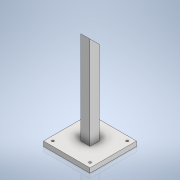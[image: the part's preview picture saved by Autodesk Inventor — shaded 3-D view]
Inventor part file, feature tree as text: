
AUTODESK INVENTOR PART (.ipt)
format: ipt  version: 2022 (Build 260153000, 153)  size: 131,584 bytes
history: native  units: mm
features: extrude x4, sketch x4
ambient origin geometry x8: Origin, YZ Plane, XZ Plane, XY Plane, X Axis, Y Axis, Z Axis, Center Point
bodies: Solid1 (feature_tree)
feature tree (8):
  extrude  "Extrusion1"  Depth=2.0mm
  extrude  "Extrusion2"  TaperAngle=45.0deg  [1 undecoded]
  extrude  "Extrusion3"  Depth=10.0mm
  extrude  "Extrusion4"  Depth=4.0mm
  sketch  "Sketch2"  dims[d5=2.0mm d6=2.0mm]
  sketch  "Sketch3"  dims[d7=20.0mm d8=0.0mm d9=45.0deg]
  sketch  "Sketch4"  dims[d10=0.0mm d11=0.0mm d12=10.0mm]
  sketch  "Sketch5"  dims[d13=10.0mm d14=4.0mm d15=4.0mm d16=1.0mm d17=0.0mm d18=0.5mm d20=9.0mm d22=1.0mm d23=20.0mm d25=8.0mm d26=20.0mm d28=8.0mm d31=0.0mm d32=0.0mm]
note: 1 required parameter value undecoded (feature->parameter linkage not recoverable at this tier; creation-order binding heuristic only, values carry confidence <= 0.55)
